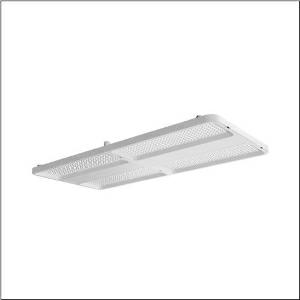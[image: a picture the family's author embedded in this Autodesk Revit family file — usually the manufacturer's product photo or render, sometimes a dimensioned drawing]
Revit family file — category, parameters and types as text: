
# Revit family: highbay_21_maxi_52hn11db4qda
name_source: partatom
category: Lighting Fixtures
units: mm (PartAtom-declared; Revit-internal decimal feet)

## family parameters
Cut with Voids When Loaded = No
Host = Face
Light Source = No
Part Type = Normal
Room Calculation Point = No
Round Connector Dimension = Use Diameter
Shared = No

## types (1)
- --- (1 x LED, 5840 lm, 31.4 W, 4000K)
    Apparent Load = 31 VA
    CIE Flux Codes = 89 97 99 100 100
    Color Rendering = 80
    Color Temperature = 4000K
    Default Elevation = 1800 mm
    Description = high bay luminaire Highbay 21 maxi; direct symmetric narrow distribution, light control with lens of PMMA; UGR ≤ 22 (X = 4H | Y = 8H | S = 0.25H | reflection values 70/50/20); luminous flux: 38.000lm; light colour: 840, colour temperature: 4000K, MacAdam ≤ 3 SDCM (initial), colour rendering: CRI > 80; luminous efficacy: 192,2lm/W; rated service life: 75.000h (L80/B50) at AT= ta max; control: DALI 2; housing frame of high-performance plastic PA6, matt traffic white (RAL 9016); cover of PMMA; dimension (LxWxH): 946 x 442 x 72mm; luminaire connection: terminal, 5-pole, max. 2.5mm² (cable entry for one cable, Ø 8.5..16mm); mains connection: 230..240V, AC/DC 0/50..60Hz; connected load: 197,7W; protection rating (complete): IP66; insulation class (complete): insulation class I (protective earthing); protection symbol: D; impact resistance: IK08; halogen-free wiring; for central battery installations according to DIN EN 60598-2-22; LABS conformity tested according to VDMA 24364:2018-05; corresponds to IFS (International Featured Standards) requirements for safety and quality in the food industry; certification: CE, ENEC, VDE, UKCA; permissible operating ambient temperature: -40..+60°C (reducing of maximum allowable ambient temperature of 5°C with ceiling mounting); packaging unit: 1 piece; (delivery without accessories; please order mounting accessories separately)
    Height = 72 mm  [stored 0.23622 ft]
    Lamp = 1 x LED
    Lamp Light Flux = 5840 lm
    Lamp Power = 31.4 W
    Lamp count = 1
    Length = 946 mm
    Luminous efficacy = 186 lm/W
    Manufacturer = Siteco
    ModVariant = No
    Model = 52HN11DB4QDA
    Mounting Place = Ceiling
    Mounting Type = Pendant
    Number of Poles = 1
    OnlyDefault = Yes
    Power Factor = 1
    Product Name = Highbay 21 maxi
    Product group = high bay luminaire
    ProductGroupID = 901
    Protection Class = Protection class I
    Protection Degree = IP 66
    RLX_Detail_Level = 1
    RLX_Emergency_Light_Flux = 0 lm
    RLX_Emergency_Type = 0
    RLX_Emergency_Type_DB = No
    RlxData = <blob elided: 23145 chars, md5=513ae63e>
    Socket = socket
    Standby Power = 0 W
    System Light Flux = 5840 lm
    System Power = 31 W
    Type Comments = : DC mode (central or group accumulator) initial emergency light level
    Type Image = l_1363244.jpg
    URL = http://relux.com
    VarID = @adj_000171
    Voltage = 0 V
    Weight = 0.00 kg
    Width = 442 mm

note: [stored X ft] marks values corroborated as IEEE doubles in the binary element streams (Revit-internal decimal feet)

## geometry (parser evidence)
native form markers: Blend x4, Sweep x11
no freeform markers — native parametric forms only
